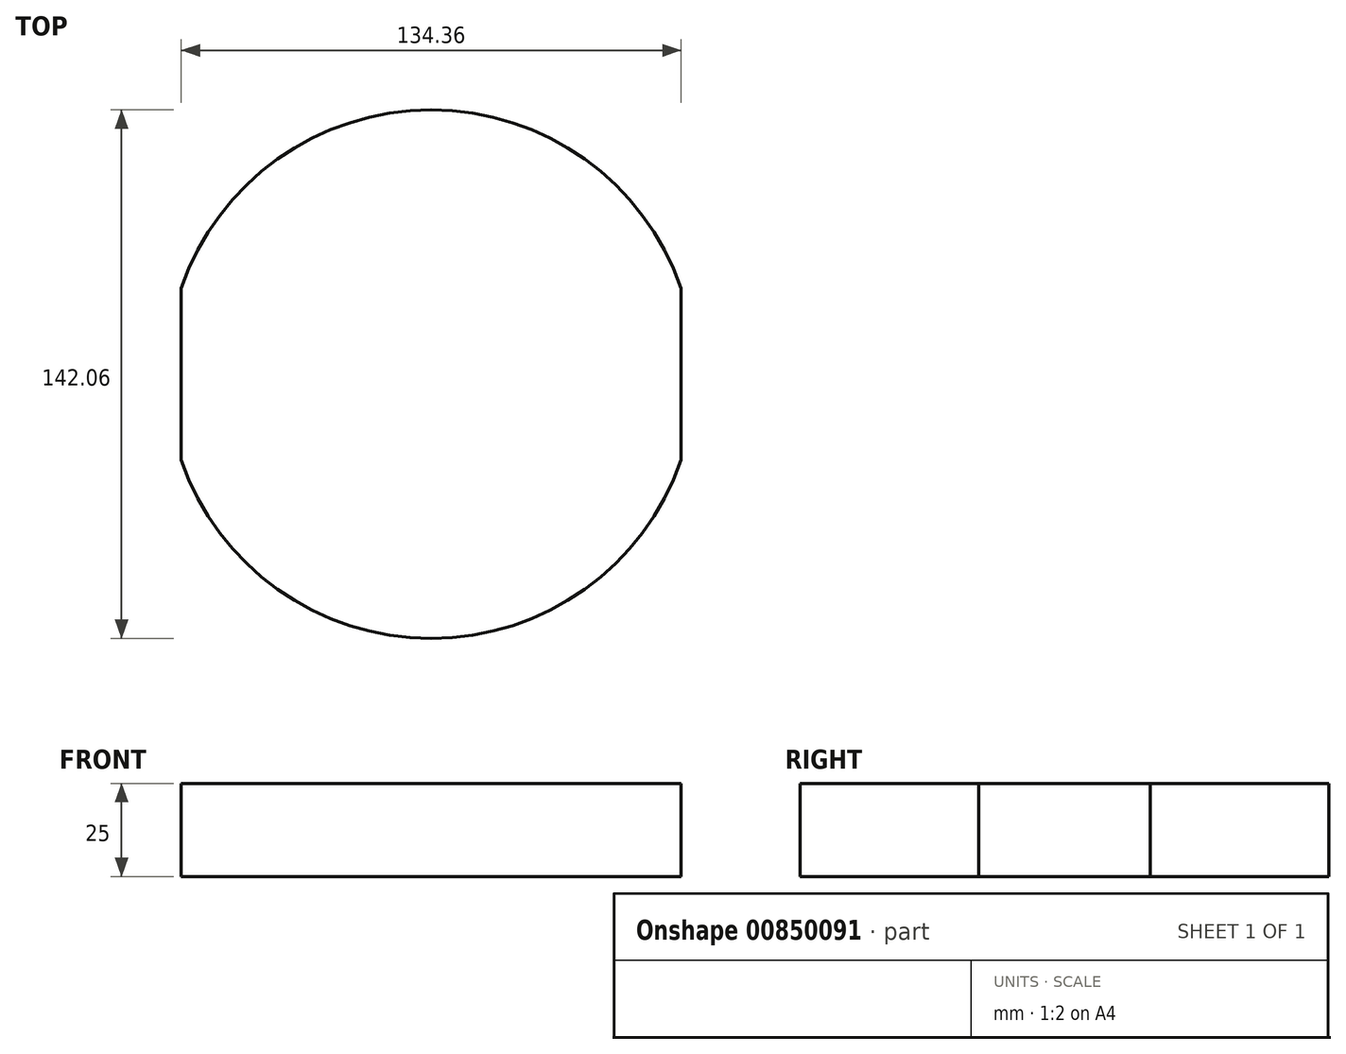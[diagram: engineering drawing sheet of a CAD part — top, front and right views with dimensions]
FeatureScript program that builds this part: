
annotation { "Feature Type Name" : "Feature", "Feature Type Description" : "" }
export const myFeature = defineFeature(function(context is Context, id is Id, definition is map)
    precondition{}
    {
        {
            var Q0;
            Q0=qCreatedBy(makeId("Top.planeOp"),FACE);
            var sketch = newSketch(context, id + "F0", { "sketchPlane" : qUnion([Q0])});
            skCircle(sketch, "E0", {"center": v(0, 0) * mm, "radius": 71.03 * mm});
            skLineSegment(sketch, "E1", {"start": v(-67.18, 36.88) * mm, "end": v(-67.18, -50.07) * mm});
            skLineSegment(sketch, "E2", {"start": v(67.18, 36.88) * mm, "end": v(67.18, -47.19) * mm});
            skSolve(sketch);
        }
        {
            var Q0;
            {var subQ0=sQuery(id+"F0.wireOp",EDGE,"E1");var subQ1=sQuery(id+"F0.wireOp",EDGE,"E0");var subQ2=makeQuery(id+"F0.imprint","INTERSECT",VERTEX,{"disambiguationData":[OD(0.0)],"derivedFrom":[subQ1,subQ0]});Q0=makeQuery(id+"F0.imprint","IMPRINT",FACE,{"disambiguationData":[TD([[makeQuery(id+"F0.imprint","IMPRINT",EDGE,{"disambiguationData":[TD([[subQ2,1.0]])],"derivedFrom":subQ1}),1.0]])]});}
            extrude(context, id + "F1", {"entities" : qUnion([Q0]), "depth" : 25 * mm, "offsetDistance" : 25 * mm});
        }
    });
